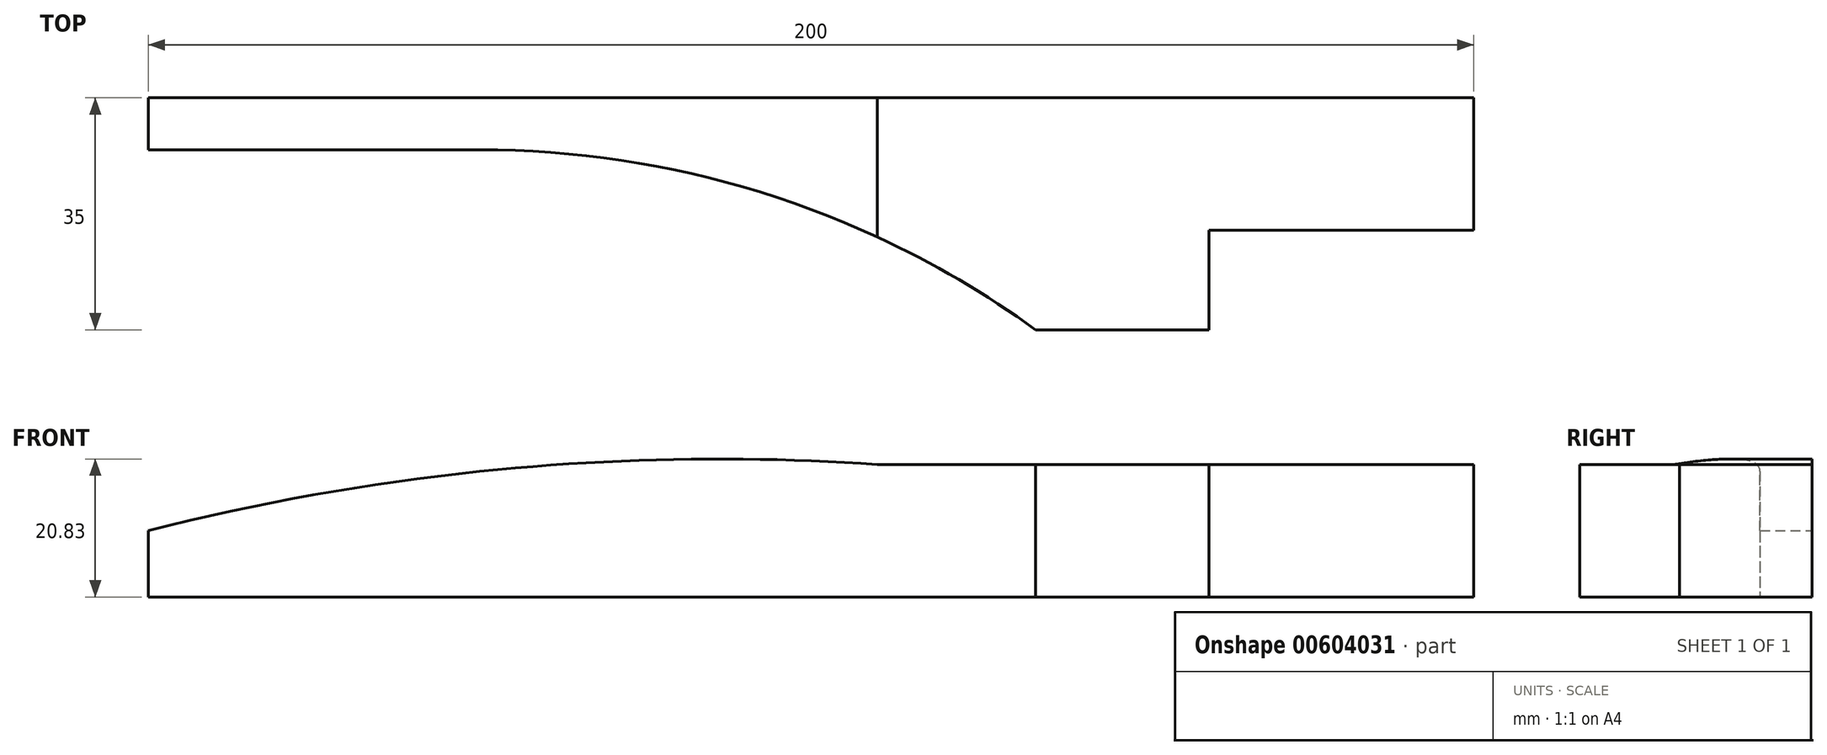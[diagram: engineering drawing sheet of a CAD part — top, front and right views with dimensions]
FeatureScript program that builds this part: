
annotation { "Feature Type Name" : "Feature", "Feature Type Description" : "" }
export const myFeature = defineFeature(function(context is Context, id is Id, definition is map)
    precondition{}
    {
        {
            var Q0;
            Q0=qCreatedBy(makeId("Front.planeOp"),FACE);
            var sketch = newSketch(context, id + "F0", { "sketchPlane" : qUnion([Q0])});
            skLineSegment(sketch, "E0", {"start": v(68.11, 0) * mm, "end": v(-131.89, 0) * mm});
            skLineSegment(sketch, "E1", {"start": v(-131.89, 0) * mm, "end": v(-131.89, 10) * mm});
            skLineSegment(sketch, "E2", {"start": v(-21.89, 20) * mm, "end": v(68.11, 20) * mm});
            skLineSegment(sketch, "E3", {"start": v(68.11, 20) * mm, "end": v(68.11, 0) * mm});
            skArc(sketch, "E4", {"start": v(-21.89, 20) * mm, "mid": v(-77.29, 19.4) * mm, "end": v(-131.89, 10) * mm});
            skSolve(sketch);
        }
        {
            var Q0;
            Q0 = qSketchRegion(id + "F0", true);
            extrude(context, id + "F1", {"entities" : qUnion([Q0]), "depth" : 35 * mm, "offsetDistance" : 25 * mm});
        }
        {
            var Q0;
            Q0=makeQuery(id+"F1.opExtrude","SWEPT_FACE",FACE,{"disambiguationData":[OSD([sQuery(id+"F0.wireOp",EDGE,"E0")])]});
            var sketch = newSketch(context, id + "F2", { "sketchPlane" : qUnion([Q0])});
            skLineSegment(sketch, "E5", {"start": v(-131.89, 7.83) * mm, "end": v(-81.89, 7.83) * mm});
            skArc(sketch, "E6", {"start": v(-81.89, 7.83) * mm, "mid": v(-37.8, 14.8) * mm, "end": v(2, 35) * mm});
            skLineSegment(sketch, "E7", {"start": v(68.11, 20) * mm, "end": v(28.11, 20) * mm});
            skLineSegment(sketch, "E8", {"start": v(28.11, 20) * mm, "end": v(28.11, 35) * mm});
            skSolve(sketch);
        }
        {
            var Q0;
            {var subQ0=sQuery(id+"F2.wireOp",EDGE,"E5");Q0=makeQuery(id+"F2.imprint","IMPRINT",FACE,{"disambiguationData":[TD([[makeQuery(id+"F2.imprint","IMPRINT",EDGE,{"derivedFrom":subQ0}),1.0]])]});}
            var Q1;
            {var subQ0=sQuery(id+"F2.wireOp",EDGE,"E7");Q1=makeQuery(id+"F2.imprint","IMPRINT",FACE,{"disambiguationData":[TD([[makeQuery(id+"F2.imprint","IMPRINT",EDGE,{"derivedFrom":subQ0}),-1.0]])]});}
            extrude(context, id + "F3", {"entities" : qUnion([Q0, Q1]), "operationType" : NewBodyOperationType.REMOVE, "oppositeDirection" : true, "depth" : 31.1 * mm, "offsetDistance" : 25 * mm});
        }
    });
